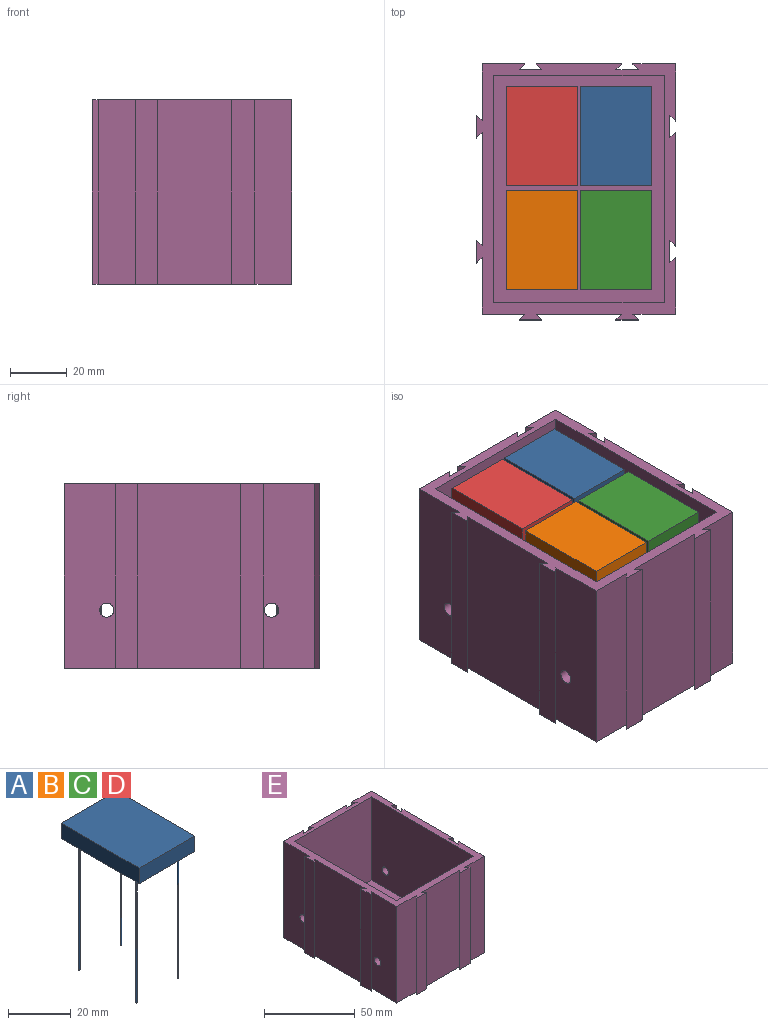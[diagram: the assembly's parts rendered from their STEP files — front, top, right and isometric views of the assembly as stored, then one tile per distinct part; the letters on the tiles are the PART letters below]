
ASSEMBLY  parts=5 mates=4
PART A: 22 faces, bbox 25x35x56 mm
  f0: plane 35x25mm, normal (0,0,-1), area 874.2mm2, adj f1,f2,f3,f4,f7,f10,f14,f19
  f1: plane 25x6mm, normal (0,-1,0), area 150mm2, adj f0,f2,f4,f5
  f2: plane 35x6mm, normal (1,0,0), area 210mm2, adj f0,f1,f3,f5
  f3: plane 25x6mm, normal (0,1,0), area 150mm2, adj f0,f2,f4,f5
  f4: plane 35x6mm, normal (-1,0,0), area 210mm2, adj f0,f1,f3,f5
  f5: plane 35x25mm, normal (0,0,1), area 875mm2, adj f1,f2,f3,f4
  f6: cylinder r=0.13mm len=50mm, axis (0,0,1), area 40.8mm2, adj f8,f9
  f7: cylinder r=0.26mm len=50mm, axis (0,0,1), area 80.1mm2, adj f0,f8
  f8: plane 0.51x0.51mm, normal (0,0,-1), area 0.2mm2, adj f6,f7
  f9: plane 0.26x0.26mm, normal (0,0,-1), area 0.1mm2, adj f6
  f10: cylinder r=0.26mm len=50mm, axis (0,0,1), area 80.1mm2, adj f0,f12
  f11: cylinder r=0.13mm len=50mm, axis (0,0,1), area 40.8mm2, adj f12,f13
  f12: plane 0.51x0.51mm, normal (0,0,-1), area 0.2mm2, adj f10,f11
  f13: plane 0.26x0.26mm, normal (0,0,-1), area 0.1mm2, adj f11
  f14: cylinder r=0.26mm len=50mm, axis (0,0,1), area 80.1mm2, adj f0,f16
  f15: cylinder r=0.13mm len=50mm, axis (0,0,1), area 40.8mm2, adj f16,f17
  f16: plane 0.51x0.51mm, normal (0,0,-1), area 0.2mm2, adj f14,f15
  f17: plane 0.26x0.26mm, normal (0,0,-1), area 0.1mm2, adj f15
  f18: cylinder r=0.13mm len=50mm, axis (0,0,1), area 40.8mm2, adj f20,f21
  f19: cylinder r=0.26mm len=50mm, axis (0,0,1), area 80.1mm2, adj f0,f20
  f20: plane 0.51x0.51mm, normal (0,0,-1), area 0.2mm2, adj f18,f19
  f21: plane 0.26x0.26mm, normal (0,0,-1), area 0.1mm2, adj f18
PART B: same geometry as A
PART C: same geometry as A
PART D: same geometry as A
PART E: 47 faces, bbox 70x90x65 mm
  f0: plane 90x70mm, normal (0,0,1), area 1183.7mm2, adj f2,f3,f4,f5,f6,f7,f8,f9
  f1: plane 90x70mm, normal (0,0,-1), area 5983.6mm2, adj f2,f3,f4,f5,f6,f7,f8,f9
  f2: plane 65x15mm, normal (0,-1,0), area 975mm2, adj f0,f1,f8,f43
  f3: plane 65x30mm, normal (0,-1,0), area 1950mm2, adj f0,f1,f44,f45
  f4: plane 65x40mm, normal (-1,0,0), area 2600mm2, adj f0,f1,f38,f39
  f5: plane 65x20mm, normal (-1,0,0), area 1280.4mm2, adj f0,f1,f6,f19,f40
  f6: plane 65x15mm, normal (0,1,0), area 975mm2, adj f0,f1,f5,f34
  f7: plane 65x30mm, normal (0,1,0), area 1950mm2, adj f0,f1,f30,f33
  f8: plane 65.01x20.02mm, normal (1,0,0), area 1281.3mm2, adj f0,f1,f2,f22,f26
  f9: plane 65.01x39.99mm, normal (1,0,0), area 2598.1mm2, adj f0,f1,f24,f27
  f10: plane 65.01x20.03mm, normal (1,0,0), area 1281.3mm2, adj f0,f1,f11,f20,f25
  f11: plane 65x15mm, normal (0,1,0), area 975mm2, adj f0,f1,f10,f31
  f12: plane 65x20mm, normal (-1,0,0), area 1280.4mm2, adj f0,f1,f13,f21,f37
  f13: plane 65x15mm, normal (0,-1,0), area 975mm2, adj f0,f1,f12,f46
  f14: plane 60x56mm, normal (0,1,0), area 3360mm2, adj f0,f15,f17,f18
  f15: plane 80x56mm, normal (-1,0,0), area 4440.7mm2, adj f0,f14,f16,f18,f20,f22
  f16: plane 60x56mm, normal (0,-1,0), area 3360mm2, adj f0,f15,f17,f18
  f17: plane 80x56mm, normal (1,0,0), area 4440.7mm2, adj f0,f14,f16,f18,f19,f21
  f18: plane 80x60mm, normal (0,0,1), area 4800mm2, adj f14,f15,f16,f17
  f19: cylinder r=2.5mm len=5mm, axis (1,0,0), area 62.8mm2, adj f5,f17
  f20: cylinder r=2.5mm len=5mm, axis (1,0,0), area 62.8mm2, adj f10,f15
  f21: cylinder r=2.5mm len=5mm, axis (1,0,0), area 62.8mm2, adj f12,f17
  f22: cylinder r=2.5mm len=5mm, axis (1,0,0), area 62.8mm2, adj f8,f15
  f23: plane 65x8mm, normal (1,0,0), area 520mm2, adj f0,f1,f24,f25
  f24: plane 65.01x2.01mm, normal (-0.71,0.71,0), area 184.1mm2, adj f0,f1,f9,f23
  f25: plane 65.01x2.01mm, normal (-0.71,-0.71,0), area 183.8mm2, adj f0,f1,f10,f23
  f26: plane 65.01x2.01mm, normal (-0.71,0.71,0), area 184.1mm2, adj f0,f1,f8,f28
  f27: plane 65.01x2.01mm, normal (-0.71,-0.71,0), area 183.8mm2, adj f0,f1,f9,f28
  f28: plane 65x8mm, normal (1,0,0), area 520mm2, adj f0,f1,f26,f27
  f29: plane 65x8mm, normal (0,1,0), area 520mm2, adj f0,f1,f30,f31
  f30: plane 65x2mm, normal (0.71,-0.71,0), area 183.8mm2, adj f0,f1,f7,f29
  f31: plane 65x2mm, normal (-0.71,-0.71,0), area 183.8mm2, adj f0,f1,f11,f29
  f32: plane 65x8mm, normal (0,1,0), area 520mm2, adj f0,f1,f33,f34
  f33: plane 65x2mm, normal (-0.71,-0.71,0), area 183.8mm2, adj f0,f1,f7,f32
  f34: plane 65x2mm, normal (0.71,-0.71,0), area 183.8mm2, adj f0,f1,f6,f32
  f35: plane 65x8mm, normal (-1,0,0), area 520mm2, adj f0,f1,f39,f40
  f36: plane 65x8mm, normal (-1,0,0), area 520mm2, adj f0,f1,f37,f38
  f37: plane 65x2mm, normal (0.71,-0.71,0), area 183.8mm2, adj f0,f1,f12,f36
  f38: plane 65x2mm, normal (0.71,0.71,0), area 183.8mm2, adj f0,f1,f4,f36
  f39: plane 65x2mm, normal (0.71,-0.71,0), area 183.8mm2, adj f0,f1,f4,f35
  f40: plane 65x2mm, normal (0.71,0.71,0), area 183.8mm2, adj f0,f1,f5,f35
  f41: plane 65x8mm, normal (0,-1,0), area 520mm2, adj f0,f1,f45,f46
  f42: plane 65x8mm, normal (0,-1,0), area 520mm2, adj f0,f1,f43,f44
  f43: plane 65x2mm, normal (0.71,0.71,0), area 183.8mm2, adj f0,f1,f2,f42
  f44: plane 65x2mm, normal (-0.71,0.71,0), area 183.8mm2, adj f0,f1,f3,f42
  f45: plane 65x2mm, normal (0.71,0.71,0), area 183.8mm2, adj f0,f1,f3,f41
  f46: plane 65x2mm, normal (-0.71,0.71,0), area 183.8mm2, adj f0,f1,f13,f41
PLACE A t=(-6.54,27.58,63.28)mm
PLACE B t=(-32.54,-9.09,63.28)mm
PLACE C t=(-6.54,-9.09,63.28)mm
PLACE D t=(-32.54,27.58,63.28)mm
PLACE E t=(-19.54,9.24,-1.72)mm
MATE fastened C.f10 <-> E.f18  axis (0,0,-1) through (2.83,-21.88,7.28)mm
MATE fastened B.f6 <-> E.f18  axis (0,0,-1) through (-41.92,-21.88,7.28)mm
MATE fastened A.f18 <-> E.f18  axis (0,0,-1) through (2.83,40.37,7.28)mm
MATE fastened D.f14 <-> E.f18  axis (0,0,-1) through (-41.92,40.37,7.28)mm
